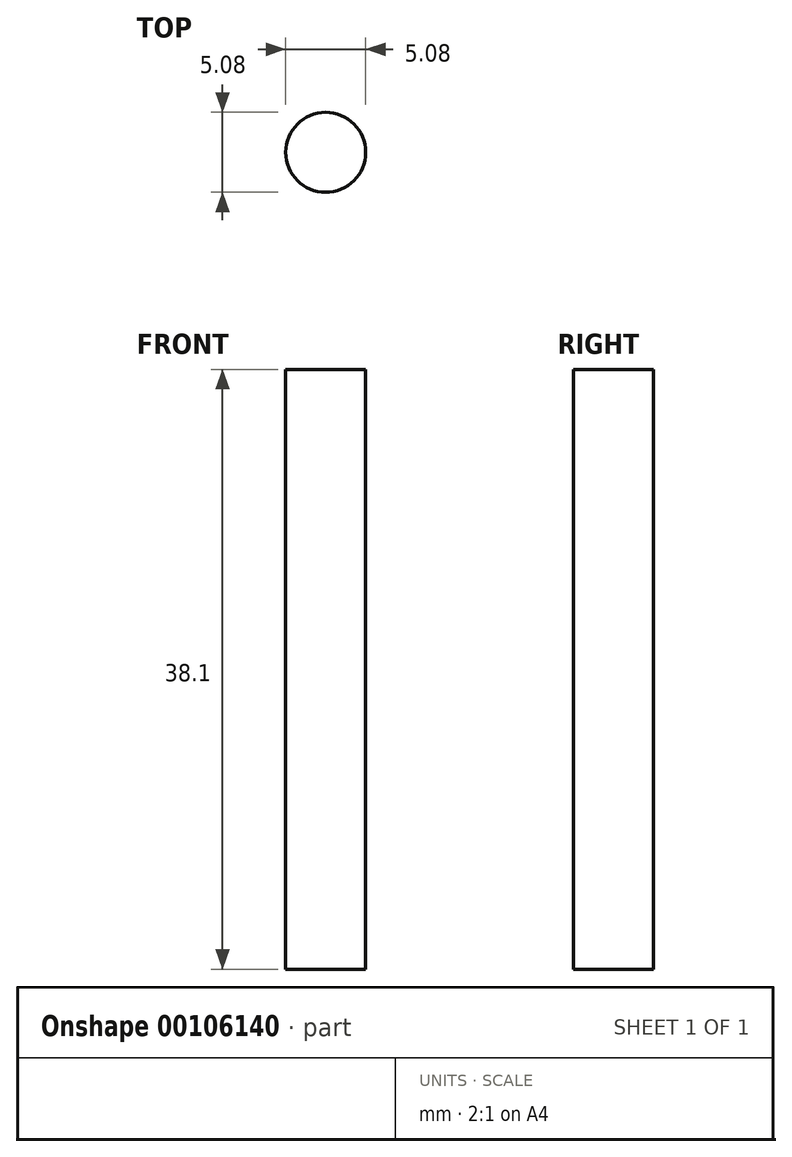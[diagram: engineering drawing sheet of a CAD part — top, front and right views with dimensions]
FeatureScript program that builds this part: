
annotation { "Feature Type Name" : "Feature", "Feature Type Description" : "" }
export const myFeature = defineFeature(function(context is Context, id is Id, definition is map)
    precondition{}
    {
        {
            var Q0;
            Q0=qCreatedBy(makeId("Top.planeOp"),FACE);
            var sketch = newSketch(context, id + "F0", { "sketchPlane" : qUnion([Q0])});
            skCircle(sketch, "E0", {"center": v(0, 0) * mm, "radius": 2.54 * mm});
            skSolve(sketch);
        }
        {
            var Q0;
            Q0 = qSketchRegion(id + "F0", true);
            extrude(context, id + "F1", {"entities" : qUnion([Q0]), "depth" : 38.1 * mm});
        }
    });
